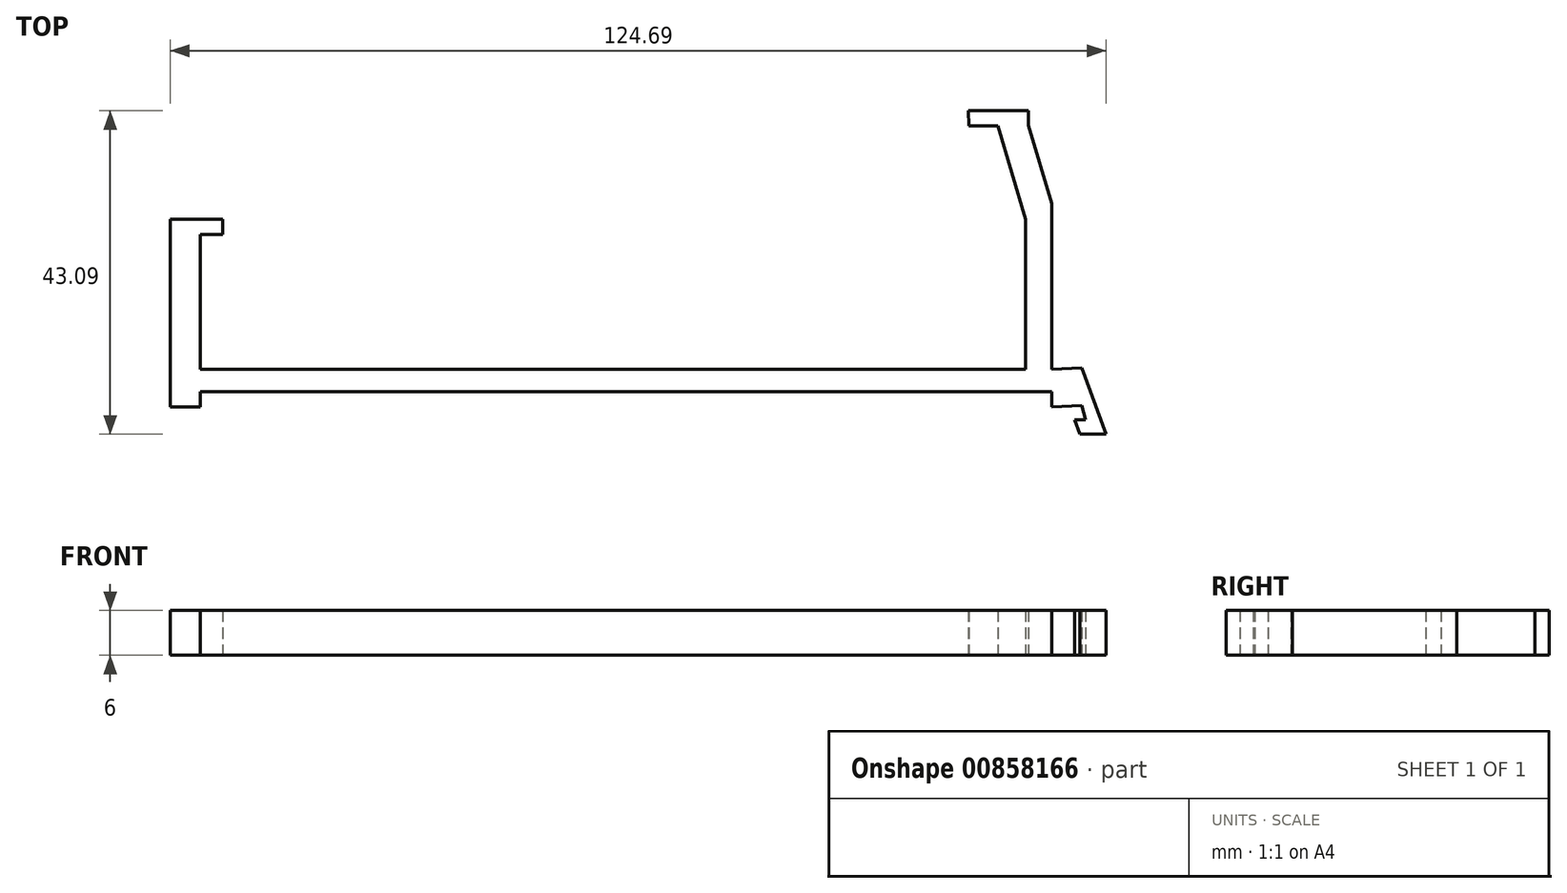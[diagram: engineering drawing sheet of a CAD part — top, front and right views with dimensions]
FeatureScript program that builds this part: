
annotation { "Feature Type Name" : "Feature", "Feature Type Description" : "" }
export const myFeature = defineFeature(function(context is Context, id is Id, definition is map)
    precondition{}
    {
        {
            var Q0;
            Q0=qCreatedBy(makeId("Top.planeOp"),FACE);
            var sketch = newSketch(context, id + "F0", { "sketchPlane" : qUnion([Q0])});
            skLineSegment(sketch, "E0.bottom", {"start": v(-40.4, -50.42) * mm, "end": v(-36.4, -50.42) * mm});
            skLineSegment(sketch, "E0.top", {"start": v(-40.4, -73.42) * mm, "end": v(-36.4, -73.42) * mm});
            skLineSegment(sketch, "E0.left", {"start": v(-40.4, -50.42) * mm, "end": v(-40.4, -73.42) * mm});
            skLineSegment(sketch, "E0.right", {"start": v(-36.4, -50.42) * mm, "end": v(-36.4, -73.42) * mm});
            skLineSegment(sketch, "E1.bottom", {"start": v(-36.4, -73.42) * mm, "end": v(77.03, -73.42) * mm});
            skLineSegment(sketch, "E1.top", {"start": v(-36.4, -70.42) * mm, "end": v(77.03, -70.42) * mm});
            skLineSegment(sketch, "E1.left", {"start": v(-36.4, -73.42) * mm, "end": v(-36.4, -70.42) * mm});
            skLineSegment(sketch, "E1.right", {"start": v(77.03, -73.42) * mm, "end": v(77.03, -70.42) * mm});
            skLineSegment(sketch, "E2.top", {"start": v(-40.4, -75.42) * mm, "end": v(-36.4, -75.42) * mm});
            skLineSegment(sketch, "E2.left", {"start": v(-40.4, -73.42) * mm, "end": v(-40.4, -75.42) * mm});
            skLineSegment(sketch, "E2.right", {"start": v(-36.4, -73.42) * mm, "end": v(-36.4, -75.42) * mm});
            skLineSegment(sketch, "E3.bottom", {"start": v(-36.4, -50.42) * mm, "end": v(-33.4, -50.42) * mm});
            skLineSegment(sketch, "E3.top", {"start": v(-36.4, -52.42) * mm, "end": v(-33.4, -52.42) * mm});
            skLineSegment(sketch, "E3.left", {"start": v(-36.4, -50.42) * mm, "end": v(-36.4, -52.42) * mm});
            skLineSegment(sketch, "E3.right", {"start": v(-33.4, -50.42) * mm, "end": v(-33.4, -52.42) * mm});
            skLineSegment(sketch, "E4.bottom", {"start": v(77.03, -70.42) * mm, "end": v(73.57, -70.42) * mm});
            skLineSegment(sketch, "E5", {"start": v(73.57, -70.42) * mm, "end": v(73.57, -50.42) * mm});
            skLineSegment(sketch, "E6", {"start": v(77.03, -70.42) * mm, "end": v(77.03, -48.3) * mm});
            skLineSegment(sketch, "E7", {"start": v(77.03, -48.3) * mm, "end": v(73.95, -37.87) * mm});
            skLineSegment(sketch, "E8", {"start": v(69.9, -37.95) * mm, "end": v(73.57, -50.42) * mm});
            skLineSegment(sketch, "E9", {"start": v(65.95, -35.95) * mm, "end": v(73.95, -35.95) * mm});
            skLineSegment(sketch, "E10", {"start": v(73.95, -35.95) * mm, "end": v(73.95, -37.87) * mm});
            skLineSegment(sketch, "E11", {"start": v(69.9, -37.95) * mm, "end": v(66, -37.95) * mm});
            skLineSegment(sketch, "E12", {"start": v(66, -37.95) * mm, "end": v(65.95, -35.95) * mm});
            skLineSegment(sketch, "E13.bottom", {"start": v(77.03, -70.42) * mm, "end": v(81.03, -70.2) * mm});
            skLineSegment(sketch, "E13.left", {"start": v(77.03, -70.42) * mm, "end": v(77.03, -73.4) * mm});
            skLineSegment(sketch, "E13.right", {"start": v(81.03, -70.2) * mm, "end": v(81.03, -73.4) * mm});
            skLineSegment(sketch, "E14", {"start": v(77.03, -73.4) * mm, "end": v(81.03, -73.4) * mm});
            skLineSegment(sketch, "E15", {"start": v(77.03, -73.4) * mm, "end": v(77.03, -75.4) * mm});
            skLineSegment(sketch, "E16", {"start": v(81.03, -73.4) * mm, "end": v(81.03, -75.25) * mm});
            skLineSegment(sketch, "E17", {"start": v(81.03, -75.25) * mm, "end": v(77.03, -75.4) * mm});
            skLineSegment(sketch, "E18", {"start": v(81.03, -75.25) * mm, "end": v(81.6, -77.17) * mm});
            skLineSegment(sketch, "E19", {"start": v(81.6, -77.17) * mm, "end": v(80.1, -77.17) * mm});
            skLineSegment(sketch, "E20", {"start": v(80.1, -77.17) * mm, "end": v(80.78, -79.04) * mm});
            skLineSegment(sketch, "E21", {"start": v(80.78, -79.04) * mm, "end": v(84.28, -79.04) * mm});
            skLineSegment(sketch, "E22", {"start": v(84.28, -79.04) * mm, "end": v(81.03, -70.2) * mm});
            skSolve(sketch);
        }
        {
            var Q0;
            {var subQ4=sQuery(id+"F0.wireOp",EDGE,"E0.bottom");Q0=makeQuery(id+"F0.imprint","IMPRINT",FACE,{"disambiguationData":[TD([[makeQuery(id+"F0.imprint","IMPRINT",EDGE,{"derivedFrom":subQ4}),-1.0]])]});}
            var Q1;
            {var subQ0=sQuery(id+"F0.wireOp",EDGE,"E13.bottom");Q1=makeQuery(id+"F0.imprint","IMPRINT",FACE,{"disambiguationData":[TD([[makeQuery(id+"F0.imprint","IMPRINT",EDGE,{"derivedFrom":subQ0}),-1.0]])]});}
            var Q2;
            {var subQ2=sQuery(id+"F0.wireOp",EDGE,"E5");Q2=makeQuery(id+"F0.imprint","IMPRINT",FACE,{"disambiguationData":[TD([[makeQuery(id+"F0.imprint","IMPRINT",EDGE,{"derivedFrom":subQ2}),-1.0]])]});}
            var Q3;
            {var subQ6=sQuery(id+"F0.wireOp",EDGE,"E1.bottom");Q3=makeQuery(id+"F0.imprint","IMPRINT",FACE,{"disambiguationData":[TD([[makeQuery(id+"F0.imprint","IMPRINT",EDGE,{"derivedFrom":subQ6}),1.0]])]});}
            var Q4;
            Q4=makeQuery(id+"F0.imprint","IMPRINT",FACE,{"disambiguationData":[TD([[makeQuery(id+"F0.imprint","IMPRINT",EDGE,{"derivedFrom":sQuery(id+"F0.wireOp",EDGE,"E0.top")}),-1.0]])]});
            var Q5;
            Q5=makeQuery(id+"F0.imprint","IMPRINT",FACE,{"disambiguationData":[TD([[makeQuery(id+"F0.imprint","IMPRINT",EDGE,{"derivedFrom":sQuery(id+"F0.wireOp",EDGE,"E13.right")}),1.0]])]});
            var Q6;
            {var subQ0=sQuery(id+"F0.wireOp",EDGE,"E3.bottom");Q6=makeQuery(id+"F0.imprint","IMPRINT",FACE,{"disambiguationData":[TD([[makeQuery(id+"F0.imprint","IMPRINT",EDGE,{"derivedFrom":subQ0}),-1.0]])]});}
            var Q7;
            {var subQ1=sQuery(id+"F0.wireOp",EDGE,"E14");Q7=makeQuery(id+"F0.imprint","IMPRINT",FACE,{"disambiguationData":[TD([[makeQuery(id+"F0.imprint","IMPRINT",EDGE,{"derivedFrom":subQ1}),-1.0]])]});}
            extrude(context, id + "F1", {"entities" : qUnion([Q0, Q1, Q2, Q3, Q4, Q5, Q6, Q7]), "depth" : 6 * mm, "offsetDistance" : 25 * mm});
        }
    });
